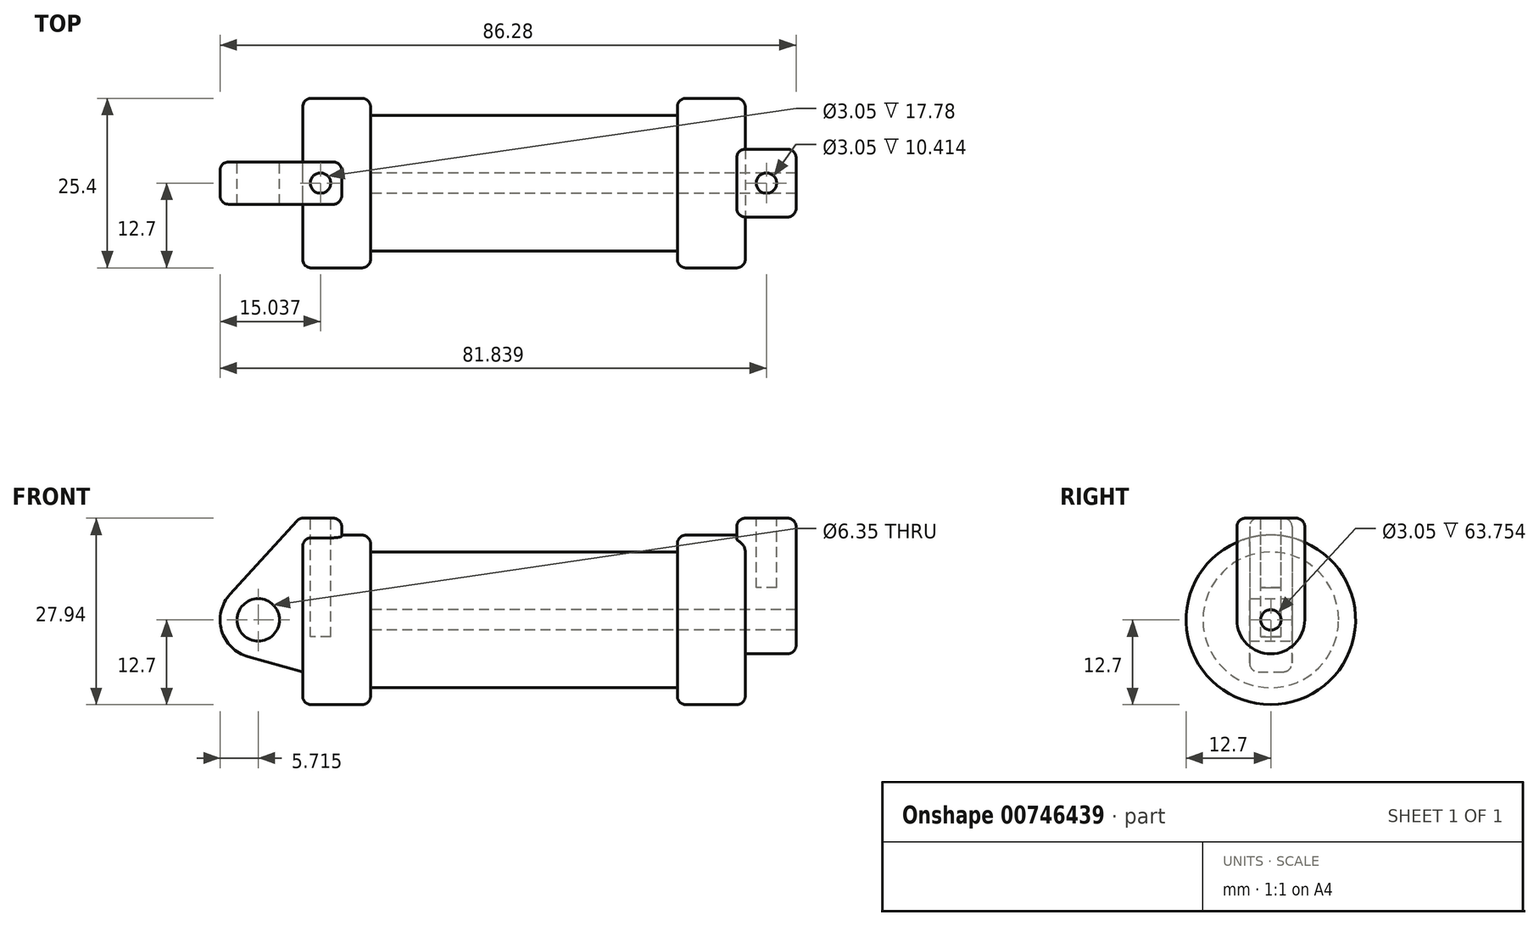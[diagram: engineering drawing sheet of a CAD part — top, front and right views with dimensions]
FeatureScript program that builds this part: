
annotation { "Feature Type Name" : "Feature", "Feature Type Description" : "" }
export const myFeature = defineFeature(function(context is Context, id is Id, definition is map)
    precondition{}
    {
        {
            var Q0;
            Q0=qCreatedBy(makeId("Front.planeOp"),FACE);
            var sketch = newSketch(context, id + "F0", { "sketchPlane" : qUnion([Q0])});
            skLineSegment(sketch, "E0", {"start": v(0, 0) * mm, "end": v(0, 12.7) * mm});
            skLineSegment(sketch, "E1", {"start": v(0, 12.7) * mm, "end": v(10.16, 12.7) * mm});
            skLineSegment(sketch, "E2", {"start": v(10.16, 12.7) * mm, "end": v(10.16, 10.16) * mm});
            skLineSegment(sketch, "E3", {"start": v(10.16, 10.16) * mm, "end": v(56.13, 10.16) * mm});
            skLineSegment(sketch, "E4", {"start": v(56.13, 10.16) * mm, "end": v(56.13, 12.7) * mm});
            skLineSegment(sketch, "E5", {"start": v(56.13, 12.7) * mm, "end": v(66.3, 12.7) * mm});
            skLineSegment(sketch, "E6", {"start": v(66.3, 12.7) * mm, "end": v(66.3, 0) * mm});
            skLineSegment(sketch, "E7", {"start": v(66.3, 0) * mm, "end": v(0, 0) * mm});
            skLineSegment(sketch, "E8", {"start": v(5.84, 15.24) * mm, "end": v(-0.5, 15.24) * mm});
            skLineSegment(sketch, "E9", {"start": v(-0.5, 15.24) * mm, "end": v(-10.88, 3.85) * mm});
            skLineSegment(sketch, "E10", {"start": v(0, 0) * mm, "end": v(-6.65, 0) * mm});
            skCircle(sketch, "E11", {"center": v(-6.65, 0) * mm, "radius": 5.72 * mm});
            skCircle(sketch, "E12", {"center": v(-6.65, 0) * mm, "radius": 3.18 * mm});
            skLineSegment(sketch, "E13", {"start": v(5.84, 15.24) * mm, "end": v(5.84, -9.4) * mm});
            skLineSegment(sketch, "E14", {"start": v(5.84, -9.4) * mm, "end": v(-8.18, -5.5) * mm});
            skSolve(sketch);
        }
        {
            var Q0;
            {var subQ0=sQuery(id+"F0.wireOp",EDGE,"E2");Q0=makeQuery(id+"F0.imprint","IMPRINT",FACE,{"disambiguationData":[TD([[makeQuery(id+"F0.imprint","IMPRINT",EDGE,{"derivedFrom":subQ0}),-1.0]])]});}
            var Q1;
            {var subQ0=sQuery(id+"F0.wireOp",EDGE,"E0");Q1=makeQuery(id+"F0.imprint","IMPRINT",FACE,{"disambiguationData":[TD([[makeQuery(id+"F0.imprint","IMPRINT",EDGE,{"derivedFrom":subQ0}),-1.0]])]});}
            var Q2;
            Q2=sQuery(id+"F0.wireOp",EDGE,"E7");
            revolve(context, id + "F1", {"surfaceOperationType" : NewSurfaceOperationType.NEW, "entities" : qUnion([Q0, Q1]), "axis" : qUnion([Q2]), "revolveType" : RevolveType.FULL});
        }
        {
            var Q0;
            {var subQ1=sQuery(id+"F0.wireOp",EDGE,"E0");Q0=makeQuery(id+"F0.imprint","IMPRINT",FACE,{"disambiguationData":[TD([[makeQuery(id+"F0.imprint","IMPRINT",EDGE,{"derivedFrom":subQ1}),1.0]])]});}
            var Q1;
            {var subQ0=sQuery(id+"F0.wireOp",EDGE,"E14");Q1=makeQuery(id+"F0.imprint","IMPRINT",FACE,{"disambiguationData":[TD([[makeQuery(id+"F0.imprint","IMPRINT",EDGE,{"derivedFrom":subQ0}),-1.0]])]});}
            var Q2;
            {var subQ5=sQuery(id+"F0.wireOp",EDGE,"E12");Q2=makeQuery(id+"F0.imprint","IMPRINT",FACE,{"disambiguationData":[TD([[makeQuery(id+"F0.imprint","IMPRINT",EDGE,{"derivedFrom":subQ5}),-1.0]])]});}
            var Q3;
            {var subQ0=sQuery(id+"F0.wireOp",EDGE,"E0");Q3=makeQuery(id+"F0.imprint","IMPRINT",FACE,{"disambiguationData":[TD([[makeQuery(id+"F0.imprint","IMPRINT",EDGE,{"derivedFrom":subQ0}),-1.0]])]});}
            extrude(context, id + "F2", {"entities" : qUnion([Q0, Q1, Q2, Q3]), "operationType" : NewBodyOperationType.ADD, "endBound" : BoundingType.SYMMETRIC, "depth" : 6.35 * mm, "offsetDistance" : 25.4 * mm});
        }
        {
            var Q0;
            Q0=makeQuery(id+"F1.opRevolve","SWEPT_FACE",FACE,{"disambiguationData":[OSD([sQuery(id+"F0.wireOp",EDGE,"E6")])]});
            var sketch = newSketch(context, id + "F3", { "sketchPlane" : qUnion([Q0])});
            skCircle(sketch, "E15", {"center": v(0, 0) * mm, "radius": 1.52 * mm});
            skCircle(sketch, "E16", {"center": v(0, 0) * mm, "radius": 5.08 * mm});
            skLineSegment(sketch, "E17", {"start": v(-5.08, 0) * mm, "end": v(-5.08, 15.24) * mm});
            skLineSegment(sketch, "E18", {"start": v(5.08, 0) * mm, "end": v(5.08, 15.24) * mm});
            skLineSegment(sketch, "E19", {"start": v(5.08, 15.24) * mm, "end": v(-5.08, 15.24) * mm});
            skSolve(sketch);
        }
        {
            var Q0;
            Q0 = qSketchRegion(id + "F3", true);
            extrude(context, id + "F4", {"entities" : qUnion([Q0]), "operationType" : NewBodyOperationType.ADD, "depth" : 7.62 * mm, "offsetDistance" : 25.4 * mm});
        }
        {
            var Q0;
            Q0=makeQuery(id+"F4.opExtrude","CAP_FACE",FACE,{"disambiguationData":[OSD([sQuery(id+"F3.wireOp",EDGE,"E15"),sQuery(id+"F3.wireOp",EDGE,"E16"),sQuery(id+"F3.wireOp",EDGE,"E17"),sQuery(id+"F3.wireOp",EDGE,"E18"),sQuery(id+"F3.wireOp",EDGE,"E19")])],"isStart":true});
            extrude(context, id + "F5", {"entities" : qUnion([Q0]), "operationType" : NewBodyOperationType.ADD, "depth" : 1.27 * mm, "offsetDistance" : 25.4 * mm});
        }
        {
            var Q0;
            Q0=makeQuery(id+"F4.boolean.opBoolean","SPLIT",FACE,{"disambiguationData":[TD([makeQuery(id+"F4.opExtrude","SWEPT_FACE",FACE,{"disambiguationData":[OSD([sQuery(id+"F3.wireOp",EDGE,"E15")])]})])],"derivedFrom":makeQuery(id+"F1.opRevolve","SWEPT_FACE",FACE,{"disambiguationData":[OSD([sQuery(id+"F0.wireOp",EDGE,"E6")])]})});
            var Q1;
            Q1=makeQuery(id+"F1.opRevolve","SWEPT_FACE",FACE,{"disambiguationData":[OSD([sQuery(id+"F0.wireOp",EDGE,"E2")])]});
            extrude(context, id + "F6", {"entities" : qUnion([Q0]), "operationType" : NewBodyOperationType.REMOVE, "endBound" : BoundingType.UP_TO_SURFACE, "oppositeDirection" : true, "depth" : 25.4 * mm, "endBoundEntityFace" : qUnion([Q1]), "offsetDistance" : 25.4 * mm});
        }
        {
            var Q0;
            {var subQ0=sQuery(id+"F3.wireOp",EDGE,"E19");Q0=makeQuery(id+"F5.boolean.opBoolean","MERGE",FACE,{"derivedFrom":[makeQuery(id+"F4.opExtrude","SWEPT_FACE",FACE,{"disambiguationData":[OSD([subQ0])]}),makeQuery(id+"F5.opExtrude","SWEPT_FACE",FACE,{"disambiguationData":[OSD([subQ0])]})]});}
            var sketch = newSketch(context, id + "F7", { "sketchPlane" : qUnion([Q0])});
            skCircle(sketch, "E20", {"center": v(69.47, 0) * mm, "radius": 1.52 * mm});
            skSolve(sketch);
        }
        {
            var Q0;
            Q0=makeQuery(id+"F2.opExtrude","SWEPT_FACE",FACE,{"disambiguationData":[OSD([sQuery(id+"F0.wireOp",EDGE,"E8")])]});
            var sketch = newSketch(context, id + "F8", { "sketchPlane" : qUnion([Q0])});
            skCircle(sketch, "E21", {"center": v(2.67, 0) * mm, "radius": 1.52 * mm});
            skSolve(sketch);
        }
        {
            var Q0;
            Q0=makeQuery(id+"F8.imprint","IMPRINT",FACE,{"disambiguationData":[TD([[makeQuery(id+"F8.imprint","IMPRINT",EDGE,{"derivedFrom":sQuery(id+"F8.wireOp",EDGE,"E21")}),1.0]])]});
            extrude(context, id + "F9", {"entities" : qUnion([Q0]), "operationType" : NewBodyOperationType.REMOVE, "oppositeDirection" : true, "depth" : 17.78 * mm, "offsetDistance" : 25.4 * mm});
        }
        {
            var Q0;
            Q0=makeQuery(id+"F7.imprint","IMPRINT",FACE,{"disambiguationData":[TD([[makeQuery(id+"F7.imprint","IMPRINT",EDGE,{"derivedFrom":sQuery(id+"F7.wireOp",EDGE,"E20")}),1.0]])]});
            extrude(context, id + "F10", {"entities" : qUnion([Q0]), "operationType" : NewBodyOperationType.REMOVE, "oppositeDirection" : true, "depth" : 10.4 * mm, "offsetDistance" : 25.4 * mm});
        }
        {
            var Q0;
            Q0=makeQuery(id+"F1.opRevolve","SWEPT_EDGE",EDGE,{"disambiguationData":[OSD([sQuery(id+"F0.wireOp",EDGE,"E1"),sQuery(id+"F0.wireOp",EDGE,"E2")])]});
            var Q1;
            Q1=makeQuery(id+"F1.opRevolve","SWEPT_EDGE",EDGE,{"disambiguationData":[OSD([sQuery(id+"F0.wireOp",EDGE,"E0"),sQuery(id+"F0.wireOp",EDGE,"E1")])]});
            var Q2;
            Q2=makeQuery(id+"F1.opRevolve","SWEPT_EDGE",EDGE,{"disambiguationData":[OSD([sQuery(id+"F0.wireOp",EDGE,"E4"),sQuery(id+"F0.wireOp",EDGE,"E5")])]});
            var Q3;
            {var subQ0=sQuery(id+"F0.wireOp",EDGE,"E5");var subQ1=sQuery(id+"F0.wireOp",EDGE,"E6");Q3=makeQuery(id+"F4.boolean.opBoolean","SPLIT",EDGE,{"disambiguationData":[topologyDisambiguationEdgeConnected([makeQuery(id+"F1.opRevolve","SWEPT_FACE",FACE,{"disambiguationData":[OSD([subQ1])]})])],"derivedFrom":makeQuery(id+"F1.opRevolve","SWEPT_EDGE",EDGE,{"disambiguationData":[OSD([subQ0,subQ1])]})});}
            fillet(context, id + "F11", {"entities" : qUnion([Q0, Q1, Q2, Q3]), "radius" : 1.27 * mm, "tangentPropagation" : true, "allowEdgeOverflow" : false});
        }
        {
            var Q0;
            Q0=makeQuery(id+"F2.opExtrude","CAP_EDGE",EDGE,{"disambiguationData":[OSD([sQuery(id+"F0.wireOp",EDGE,"E8")])],"isStart":true});
            var Q1;
            Q1=makeQuery(id+"F2.opExtrude","SWEPT_EDGE",EDGE,{"disambiguationData":[OSD([sQuery(id+"F0.wireOp",EDGE,"E8"),sQuery(id+"F0.wireOp",EDGE,"E13")])]});
            var Q2;
            Q2=makeQuery(id+"F2.opExtrude","CAP_EDGE",EDGE,{"disambiguationData":[OSD([sQuery(id+"F0.wireOp",EDGE,"E8")])],"isStart":false});
            var Q3;
            Q3=makeQuery(id+"F2.opExtrude","SWEPT_EDGE",EDGE,{"disambiguationData":[OSD([sQuery(id+"F0.wireOp",EDGE,"E8"),sQuery(id+"F0.wireOp",EDGE,"E9")])]});
            var Q4;
            Q4=makeQuery(id+"F2.opExtrude","CAP_EDGE",EDGE,{"disambiguationData":[OSD([sQuery(id+"F0.wireOp",EDGE,"E13")])],"isStart":true});
            var Q5;
            Q5=makeQuery(id+"F2.opExtrude","CAP_EDGE",EDGE,{"disambiguationData":[OSD([sQuery(id+"F0.wireOp",EDGE,"E13")])],"isStart":false});
            var Q6;
            Q6=makeQuery(id+"F2.opExtrude","CAP_EDGE",EDGE,{"disambiguationData":[OSD([sQuery(id+"F0.wireOp",EDGE,"E9")])],"isStart":false});
            var Q7;
            Q7=makeQuery(id+"F2.opExtrude","CAP_EDGE",EDGE,{"disambiguationData":[OSD([sQuery(id+"F0.wireOp",EDGE,"E9")])],"isStart":true});
            var Q8;
            Q8=makeQuery(id+"F2.opExtrude","CAP_EDGE",EDGE,{"disambiguationData":[OSD([sQuery(id+"F0.wireOp",EDGE,"E11")])],"isStart":false});
            var Q9;
            Q9=makeQuery(id+"F2.opExtrude","CAP_EDGE",EDGE,{"disambiguationData":[OSD([sQuery(id+"F0.wireOp",EDGE,"E11")])],"isStart":true});
            var Q10;
            Q10=makeQuery(id+"F2.opExtrude","CAP_EDGE",EDGE,{"disambiguationData":[OSD([sQuery(id+"F0.wireOp",EDGE,"E14")])],"isStart":false});
            var Q11;
            Q11=makeQuery(id+"F2.opExtrude","CAP_EDGE",EDGE,{"disambiguationData":[OSD([sQuery(id+"F0.wireOp",EDGE,"E14")])],"isStart":true});
            fillet(context, id + "F12", {"entities" : qUnion([Q0, Q1, Q2, Q3, Q4, Q5, Q6, Q7, Q8, Q9, Q10, Q11]), "radius" : 1.27 * mm, "tangentPropagation" : true, "allowEdgeOverflow" : false});
        }
        {
            var Q0;
            Q0=makeQuery(id+"F5.opExtrude","CAP_EDGE",EDGE,{"disambiguationData":[OSD([sQuery(id+"F3.wireOp",EDGE,"E19")])],"isStart":false});
            var Q1;
            {var subQ0=sQuery(id+"F3.wireOp",EDGE,"E19");var subQ1=sQuery(id+"F3.wireOp",EDGE,"E17");Q1=makeQuery(id+"F5.boolean.opBoolean","MERGE",EDGE,{"derivedFrom":[makeQuery(id+"F4.opExtrude","SWEPT_EDGE",EDGE,{"disambiguationData":[OSD([subQ1,subQ0])]}),makeQuery(id+"F5.opExtrude","SWEPT_EDGE",EDGE,{"disambiguationData":[OSD([subQ1,subQ0])]})]});}
            var Q2;
            {var subQ0=sQuery(id+"F3.wireOp",EDGE,"E19");var subQ1=sQuery(id+"F3.wireOp",EDGE,"E18");Q2=makeQuery(id+"F5.boolean.opBoolean","MERGE",EDGE,{"derivedFrom":[makeQuery(id+"F4.opExtrude","SWEPT_EDGE",EDGE,{"disambiguationData":[OSD([subQ1,subQ0])]}),makeQuery(id+"F5.opExtrude","SWEPT_EDGE",EDGE,{"disambiguationData":[OSD([subQ1,subQ0])]})]});}
            var Q3;
            Q3=makeQuery(id+"F5.opExtrude","CAP_EDGE",EDGE,{"disambiguationData":[OSD([sQuery(id+"F3.wireOp",EDGE,"E17")])],"isStart":false});
            var Q4;
            Q4=makeQuery(id+"F4.opExtrude","CAP_EDGE",EDGE,{"disambiguationData":[OSD([sQuery(id+"F3.wireOp",EDGE,"E17")])],"isStart":false});
            var Q5;
            Q5=makeQuery(id+"F4.opExtrude","CAP_EDGE",EDGE,{"disambiguationData":[OSD([sQuery(id+"F3.wireOp",EDGE,"E18")])],"isStart":false});
            var Q6;
            Q6=makeQuery(id+"F5.opExtrude","CAP_EDGE",EDGE,{"disambiguationData":[OSD([sQuery(id+"F3.wireOp",EDGE,"E18")])],"isStart":false});
            var Q7;
            Q7=makeQuery(id+"F4.opExtrude","CAP_EDGE",EDGE,{"disambiguationData":[OSD([sQuery(id+"F3.wireOp",EDGE,"E16")])],"isStart":false});
            var Q8;
            Q8=makeQuery(id+"F4.opExtrude","CAP_EDGE",EDGE,{"disambiguationData":[OSD([sQuery(id+"F3.wireOp",EDGE,"E19")])],"isStart":false});
            fillet(context, id + "F13", {"entities" : qUnion([Q0, Q1, Q2, Q3, Q4, Q5, Q6, Q7, Q8]), "radius" : 1.27 * mm, "tangentPropagation" : true, "allowEdgeOverflow" : false});
        }
    });
